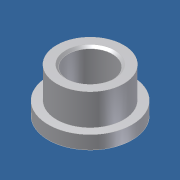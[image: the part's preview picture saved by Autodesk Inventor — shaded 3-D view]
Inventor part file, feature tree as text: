
AUTODESK INVENTOR PART (.ipt)
format: ipt  version: unknown  size: 192,512 bytes
history: native  units: in
note: dims shown in document units (in); Inventor stores cm internally (conversion verified against a paired STEP export)
features: revolve x1, chamfer x1, fillet x1, sketch x1
ambient origin geometry x8: Origin, YZ Plane, XZ Plane, XY Plane, X Axis, Y Axis, Z Axis, Center Point
bodies: Solid1 (feature_tree)
feature tree (4):
  revolve  "Revolution1"  [1 undecoded]
  chamfer  "Chamfer1"  Distance=0.375in
  fillet  "Fillet1"  Radius=0.25in
  sketch  "Sketch1"  dims[d0=0.5in d1=0.469in d2=0.375in d3=0.25in d4=0.15in d5=90.0deg d6=0.025in d7=0.125in d8=45.0deg d9=0.005in]
note: 1 required parameter value undecoded (feature->parameter linkage not recoverable at this tier; creation-order binding heuristic only, values carry confidence <= 0.55)
